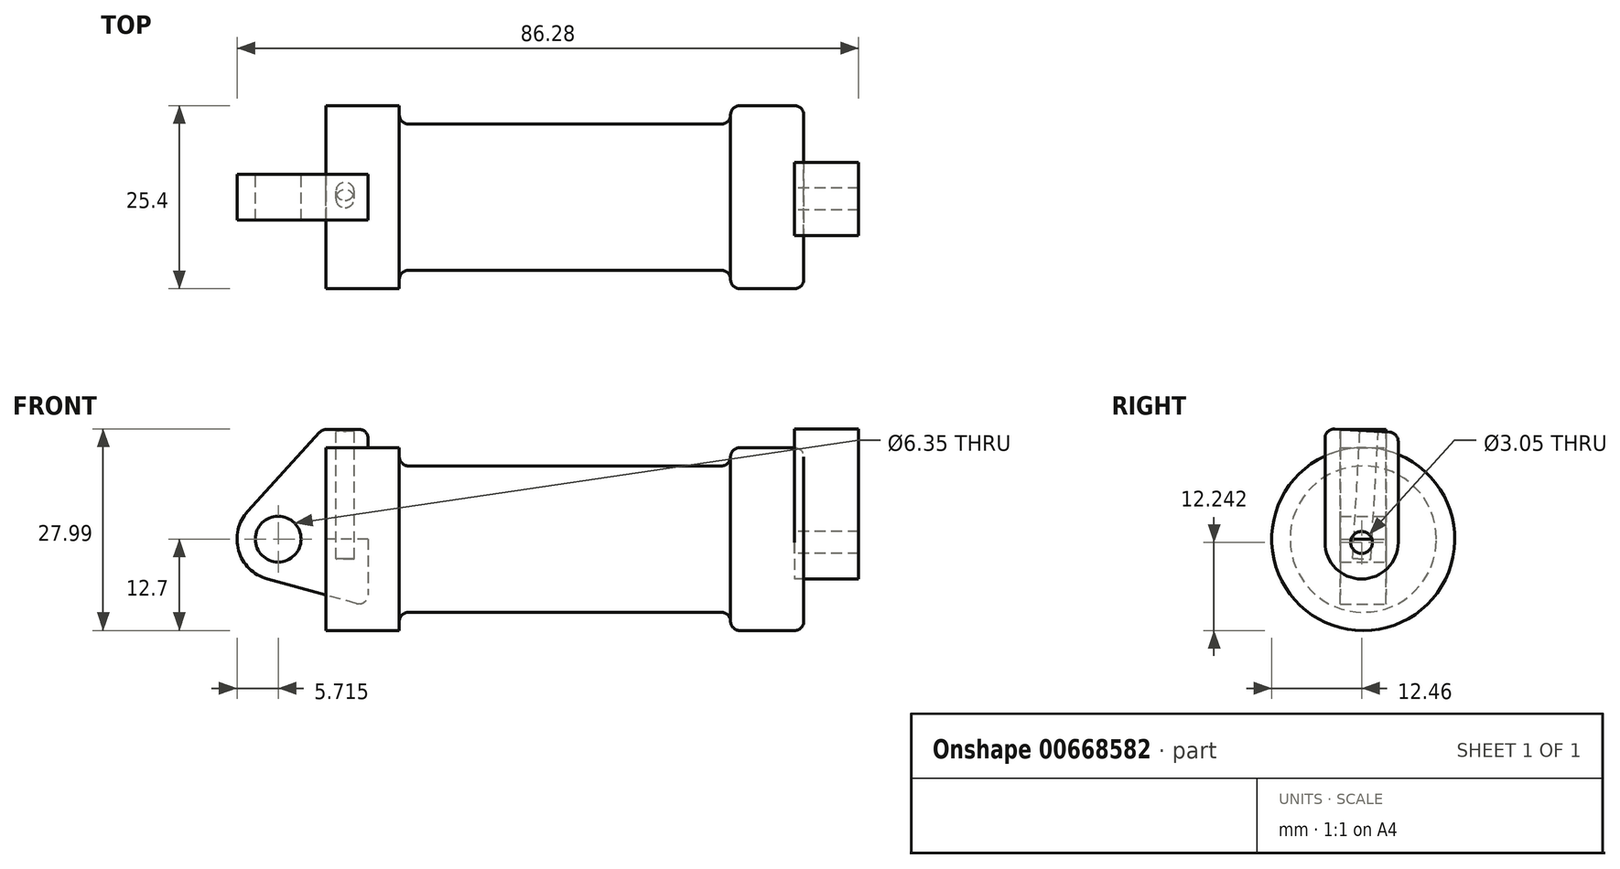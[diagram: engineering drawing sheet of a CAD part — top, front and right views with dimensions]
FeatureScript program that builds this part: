
annotation { "Feature Type Name" : "Feature", "Feature Type Description" : "" }
export const myFeature = defineFeature(function(context is Context, id is Id, definition is map)
    precondition{}
    {
        {
            var Q0;
            Q0=qCreatedBy(makeId("Front.planeOp"),FACE);
            var sketch = newSketch(context, id + "F0", { "sketchPlane" : qUnion([Q0])});
            skLineSegment(sketch, "E0", {"start": v(0, 0) * mm, "end": v(0, 12.7) * mm});
            skLineSegment(sketch, "E1", {"start": v(0, 12.7) * mm, "end": v(10.16, 12.7) * mm});
            skLineSegment(sketch, "E2", {"start": v(10.16, 12.7) * mm, "end": v(10.16, 11.43) * mm});
            skLineSegment(sketch, "E3", {"start": v(11.43, 10.16) * mm, "end": v(54.86, 10.16) * mm});
            skLineSegment(sketch, "E4", {"start": v(56.13, 11.43) * mm, "end": v(56.13, 11.43) * mm});
            skLineSegment(sketch, "E5", {"start": v(57.4, 12.7) * mm, "end": v(65.02, 12.7) * mm});
            skLineSegment(sketch, "E6", {"start": v(66.3, 11.43) * mm, "end": v(66.3, 1.27) * mm});
            skLineSegment(sketch, "E7", {"start": v(65.02, 0) * mm, "end": v(0, 0) * mm});
            skLineSegment(sketch, "E8", {"start": v(4.57, 15.24) * mm, "end": v(0.05, 15.24) * mm});
            skLineSegment(sketch, "E9", {"start": v(-0.89, 14.83) * mm, "end": v(-10.88, 3.85) * mm});
            skLineSegment(sketch, "E10", {"start": v(0, 0) * mm, "end": v(-6.65, 0) * mm});
            skCircle(sketch, "E11", {"center": v(-6.65, 0) * mm, "radius": 5.72 * mm});
            skCircle(sketch, "E12", {"center": v(-6.65, 0) * mm, "radius": 3.18 * mm});
            skLineSegment(sketch, "E13", {"start": v(5.84, 13.97) * mm, "end": v(5.84, -7.73) * mm});
            skLineSegment(sketch, "E14", {"start": v(4.23, -8.95) * mm, "end": v(-8.18, -5.5) * mm});
            skPoint(sketch, "E15.visualSharp", {"position": v(66.3, 12.7) * mm});
            skArc(sketch, "E15.filletArc", {"start": v(66.3, 11.43) * mm, "mid": v(65.92, 12.33) * mm, "end": v(65.02, 12.7) * mm});
            skPoint(sketch, "E16.visualSharp", {"position": v(56.13, 12.7) * mm});
            skArc(sketch, "E16.filletArc", {"start": v(57.4, 12.7) * mm, "mid": v(56.5, 12.33) * mm, "end": v(56.13, 11.43) * mm});
            skPoint(sketch, "E17.visualSharp", {"position": v(56.13, 10.16) * mm});
            skArc(sketch, "E17.filletArc", {"start": v(54.86, 10.16) * mm, "mid": v(55.76, 10.53) * mm, "end": v(56.13, 11.43) * mm});
            skPoint(sketch, "E18.visualSharp", {"position": v(66.3, 0) * mm});
            skArc(sketch, "E18.filletArc", {"start": v(65.02, 0) * mm, "mid": v(65.92, 0.37) * mm, "end": v(66.3, 1.27) * mm});
            skPoint(sketch, "E19.visualSharp", {"position": v(10.16, 10.16) * mm});
            skArc(sketch, "E19.filletArc", {"start": v(10.16, 11.43) * mm, "mid": v(10.53, 10.53) * mm, "end": v(11.43, 10.16) * mm});
            skPoint(sketch, "E20.visualSharp", {"position": v(5.84, 15.24) * mm});
            skArc(sketch, "E20.filletArc", {"start": v(5.84, 13.97) * mm, "mid": v(5.47, 14.87) * mm, "end": v(4.57, 15.24) * mm});
            skPoint(sketch, "E21.visualSharp", {"position": v(-0.5, 15.24) * mm});
            skArc(sketch, "E21.filletArc", {"start": v(0.05, 15.24) * mm, "mid": v(-0.46, 15.13) * mm, "end": v(-0.89, 14.83) * mm});
            skPoint(sketch, "E22.visualSharp", {"position": v(5.84, -9.4) * mm});
            skArc(sketch, "E22.filletArc", {"start": v(4.23, -8.95) * mm, "mid": v(5.34, -8.74) * mm, "end": v(5.84, -7.73) * mm});
            skText(sketch, "E23", { "text": "Nicole Volume: 1.729 in cubed ", "fontName": "OpenSans-Regular.ttf"});
            const initialGuessF0  = {"E23": [0.02456, 0.01951, 1, 0, 0.0092]};
            skSetInitialGuess(sketch, initialGuessF0);
            skSolve(sketch);
        }
        {
            var Q0;
            {var subQ0=sQuery(id+"F0.wireOp",EDGE,"E14");Q0=makeQuery(id+"F0.imprint","IMPRINT",FACE,{"disambiguationData":[TD([[makeQuery(id+"F0.imprint","IMPRINT",EDGE,{"derivedFrom":subQ0}),-1.0]])]});}
            var Q1;
            {var subQ5=sQuery(id+"F0.wireOp",EDGE,"E12");Q1=makeQuery(id+"F0.imprint","IMPRINT",FACE,{"disambiguationData":[TD([[makeQuery(id+"F0.imprint","IMPRINT",EDGE,{"derivedFrom":subQ5}),-1.0]])]});}
            var Q2;
            {var subQ1=sQuery(id+"F0.wireOp",EDGE,"E0");Q2=makeQuery(id+"F0.imprint","IMPRINT",FACE,{"disambiguationData":[TD([[makeQuery(id+"F0.imprint","IMPRINT",EDGE,{"derivedFrom":subQ1}),1.0]])]});}
            extrude(context, id + "F1", {"entities" : qUnion([Q0, Q1, Q2]), "endBound" : BoundingType.SYMMETRIC, "depth" : 6.35 * mm, "offsetDistance" : 25.4 * mm});
        }
        {
            var Q0;
            {var subQ0=sQuery(id+"F0.wireOp",EDGE,"E0");Q0=makeQuery(id+"F0.imprint","IMPRINT",FACE,{"disambiguationData":[TD([[makeQuery(id+"F0.imprint","IMPRINT",EDGE,{"derivedFrom":subQ0}),-1.0]])]});}
            var Q1;
            {var subQ0=sQuery(id+"F0.wireOp",EDGE,"E2");Q1=makeQuery(id+"F0.imprint","IMPRINT",FACE,{"disambiguationData":[TD([[makeQuery(id+"F0.imprint","IMPRINT",EDGE,{"derivedFrom":subQ0}),-1.0]])]});}
            var Q2;
            Q2=sQuery(id+"F0.wireOp",EDGE,"E7");
            revolve(context, id + "F2", {"entities" : qUnion([Q0, Q1]), "axis" : qUnion([Q2]), "revolveType" : RevolveType.FULL});
        }
        {
            var Q0;
            Q0=makeQuery(id+"F2.opRevolve","SWEPT_FACE",FACE,{"disambiguationData":[OSD([sQuery(id+"F0.wireOp",EDGE,"E6")])]});
            var sketch = newSketch(context, id + "F3", { "sketchPlane" : qUnion([Q0])});
            skCircle(sketch, "E24", {"center": v(-0.24, -0.46) * mm, "radius": 1.52 * mm});
            skCircle(sketch, "E25", {"center": v(-0.24, -0.46) * mm, "radius": 5.08 * mm});
            skLineSegment(sketch, "E26", {"start": v(4.84, -0.46) * mm, "end": v(4.84, 13.59) * mm});
            skLineSegment(sketch, "E27", {"start": v(-5.32, -0.46) * mm, "end": v(-5.32, 14.02) * mm});
            skLineSegment(sketch, "E28", {"start": v(-3.98, 15.29) * mm, "end": v(3.64, 14.85) * mm});
            skPoint(sketch, "E29.visualSharp", {"position": v(4.84, 14.79) * mm});
            skArc(sketch, "E29.filletArc", {"start": v(4.84, 13.59) * mm, "mid": v(4.5, 14.46) * mm, "end": v(3.64, 14.85) * mm});
            skPoint(sketch, "E30.visualSharp", {"position": v(-5.32, 15.36) * mm});
            skArc(sketch, "E30.filletArc", {"start": v(-3.98, 15.29) * mm, "mid": v(-4.92, 14.94) * mm, "end": v(-5.32, 14.02) * mm});
            skSolve(sketch);
        }
        {
            var Q0;
            Q0 = qSketchRegion(id + "F3", true);
            extrude(context, id + "F4", {"entities" : qUnion([Q0]), "depth" : 7.62 * mm, "offsetDistance" : 25.4 * mm, "hasSecondDirection" : true, "secondDirectionOppositeDirection" : true, "secondDirectionDepth" : 1.27 * mm});
        }
        {
            var Q0;
            Q0=makeQuery(id+"F4.opExtrude","SWEPT_FACE",FACE,{"disambiguationData":[OSD([sQuery(id+"F3.wireOp",EDGE,"E28")])]});
            var sketch = newSketch(context, id + "F5", { "sketchPlane" : qUnion([Q0])});
            skCircle(sketch, "E31", {"center": v(69.56, -0.1) * mm, "radius": 1.52 * mm});
            skCircle(sketch, "E32", {"center": v(2.62, -0.05) * mm, "radius": 1.26 * mm});
            skSolve(sketch);
        }
        {
            var Q0;
            Q0=makeQuery(id+"F5.imprint","IMPRINT",FACE,{"disambiguationData":[TD([[makeQuery(id+"F5.imprint","IMPRINT",EDGE,{"derivedFrom":sQuery(id+"F5.wireOp",EDGE,"E32")}),1.0]])]});
            var Q1;
            Q1=sQuery(id+"F5.wireOp",EDGE,"E32");
            extrude(context, id + "F6", {"entities" : qUnion([Q0]), "surfaceEntities" : qUnion([Q1]), "oppositeDirection" : true, "depth" : 17.78 * mm, "offsetDistance" : 25.4 * mm});
        }
        {
            var Q0;
            Q0=sQuery(id+"F5.wireOp",EDGE,"E31");
            extrude(context, id + "F7", {"bodyType" : ToolBodyType.SURFACE, "surfaceEntities" : qUnion([Q0]), "oppositeDirection" : true, "depth" : 10.4 * mm, "offsetDistance" : 25.4 * mm});
        }
    });
